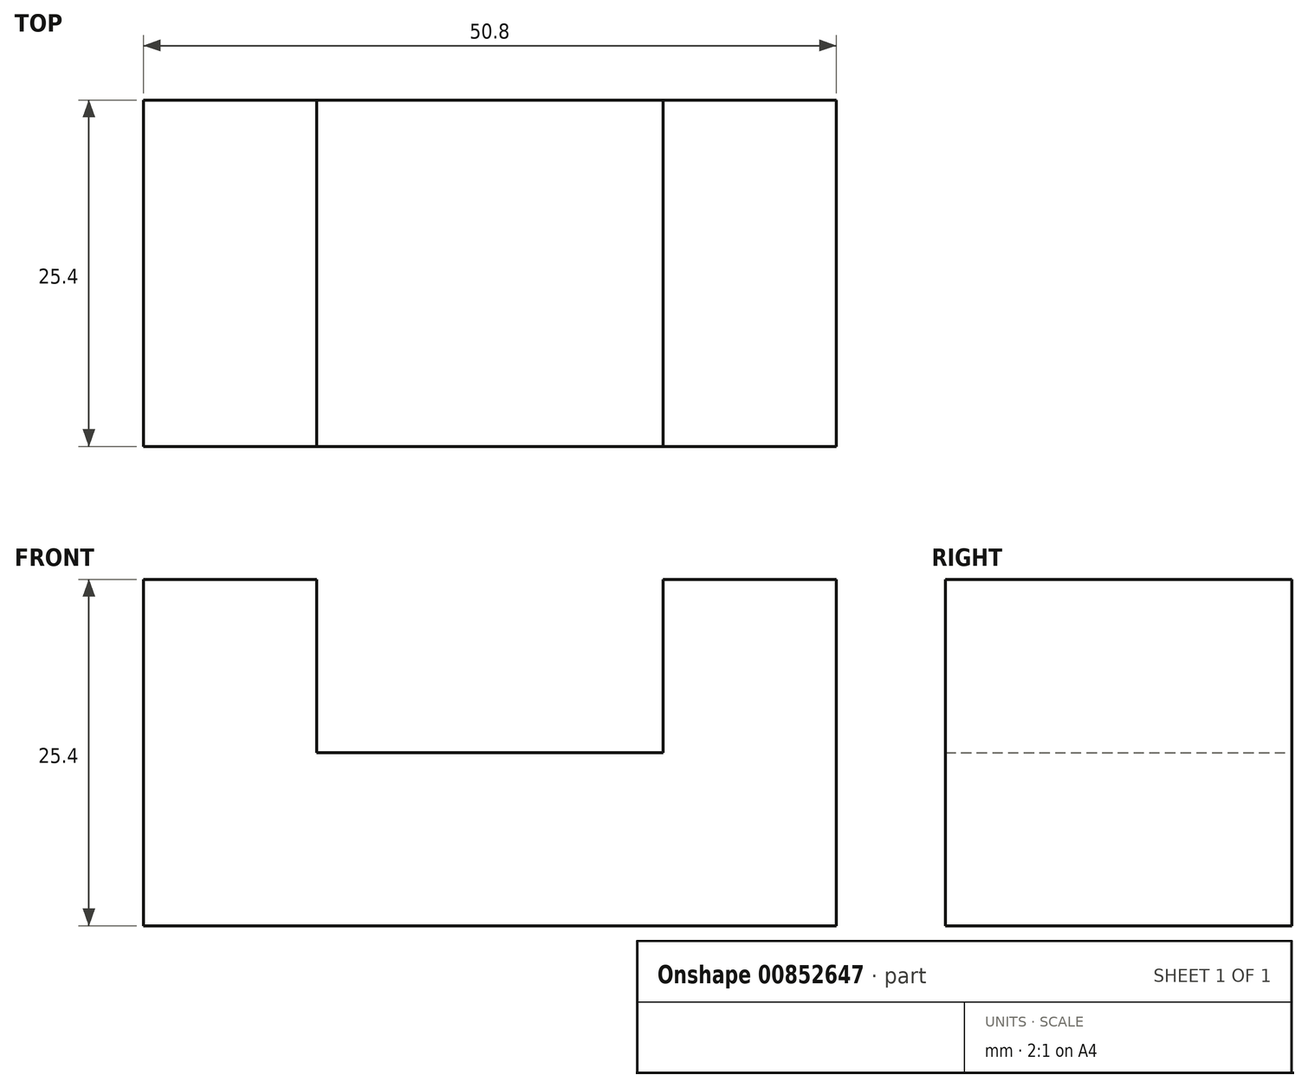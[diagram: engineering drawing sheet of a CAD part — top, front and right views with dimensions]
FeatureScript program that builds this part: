
annotation { "Feature Type Name" : "Feature", "Feature Type Description" : "" }
export const myFeature = defineFeature(function(context is Context, id is Id, definition is map)
    precondition{}
    {
        {
            var Q0;
            Q0=qCreatedBy(makeId("Front.planeOp"),FACE);
            var sketch = newSketch(context, id + "F0", { "sketchPlane" : qUnion([Q0])});
            skLineSegment(sketch, "E0", {"start": v(-25.4, 25.4) * mm, "end": v(-25.4, 0) * mm});
            skLineSegment(sketch, "E1", {"start": v(-25.4, 0) * mm, "end": v(25.4, 0) * mm});
            skLineSegment(sketch, "E2", {"start": v(25.4, 0) * mm, "end": v(25.4, 25.4) * mm});
            skLineSegment(sketch, "E3", {"start": v(25.4, 25.4) * mm, "end": v(12.7, 25.4) * mm});
            skLineSegment(sketch, "E4", {"start": v(12.7, 25.4) * mm, "end": v(12.7, 12.7) * mm});
            skLineSegment(sketch, "E5", {"start": v(12.7, 12.7) * mm, "end": v(-12.7, 12.7) * mm});
            skLineSegment(sketch, "E6", {"start": v(-12.7, 12.7) * mm, "end": v(-12.7, 25.4) * mm});
            skLineSegment(sketch, "E7", {"start": v(-12.7, 25.4) * mm, "end": v(-25.4, 25.4) * mm});
            skLineSegment(sketch, "E8", {"start": v(0, 0) * mm, "end": v(0, -3.72) * mm, "construction": true});
            skSolve(sketch);
        }
        {
            var Q0;
            Q0=makeQuery(id+"F0.imprint","IMPRINT",FACE,{"disambiguationData":[TD([[makeQuery(id+"F0.imprint","IMPRINT",EDGE,{"derivedFrom":sQuery(id+"F0.wireOp",EDGE,"E0")}),1.0]])]});
            extrude(context, id + "F1", {"entities" : qUnion([Q0]), "endBound" : BoundingType.SYMMETRIC, "depth" : 25.4 * mm, "offsetDistance" : 25.4 * mm});
        }
    });
